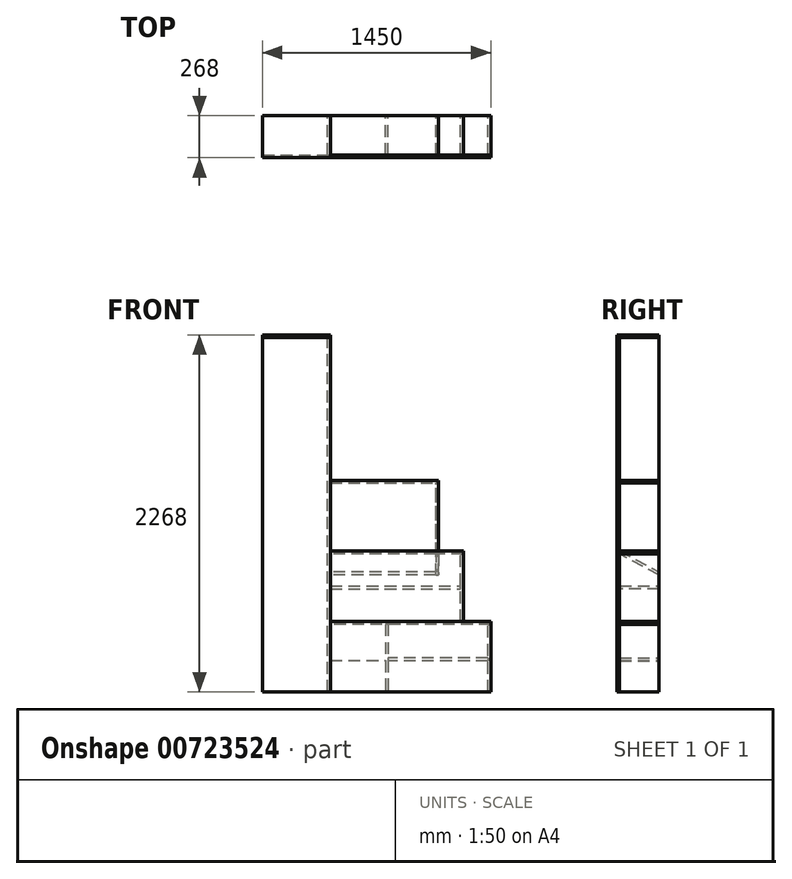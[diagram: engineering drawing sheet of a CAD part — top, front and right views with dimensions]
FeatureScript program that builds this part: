
annotation { "Feature Type Name" : "Feature", "Feature Type Description" : "" }
export const myFeature = defineFeature(function(context is Context, id is Id, definition is map)
    precondition{}
    {
        {
            var Q0;
            Q0=qCreatedBy(makeId("Front.planeOp"),FACE);
            var sketch = newSketch(context, id + "F0", { "sketchPlane" : qUnion([Q0])});
            skLineSegment(sketch, "E0.bottom", {"start": v(0, 0) * mm, "end": v(430, 0) * mm});
            skLineSegment(sketch, "E0.top", {"start": v(0, 2250) * mm, "end": v(430, 2250) * mm});
            skLineSegment(sketch, "E0.left", {"start": v(0, 0) * mm, "end": v(0, 2250) * mm});
            skLineSegment(sketch, "E0.right", {"start": v(430, 0) * mm, "end": v(430, 2250) * mm});
            skSolve(sketch);
        }
        {
            var Q0;
            Q0=qCreatedBy(makeId("Front.planeOp"),FACE);
            var sketch = newSketch(context, id + "F1", { "sketchPlane" : qUnion([Q0])});
            skLineSegment(sketch, "E1.bottom", {"start": v(430, 0) * mm, "end": v(1450, 0) * mm});
            skLineSegment(sketch, "E1.top", {"start": v(430, 448) * mm, "end": v(1450, 448) * mm});
            skLineSegment(sketch, "E1.left", {"start": v(430, 0) * mm, "end": v(430, 448) * mm});
            skLineSegment(sketch, "E1.right", {"start": v(1450, 0) * mm, "end": v(1450, 448) * mm});
            skSolve(sketch);
        }
        {
            var Q0;
            Q0=qCreatedBy(makeId("Front.planeOp"),FACE);
            var sketch = newSketch(context, id + "F2", { "sketchPlane" : qUnion([Q0])});
            skLineSegment(sketch, "E2.bottom", {"start": v(430, 448) * mm, "end": v(1275, 448) * mm});
            skLineSegment(sketch, "E2.top", {"start": v(430, 896) * mm, "end": v(1275, 896) * mm});
            skLineSegment(sketch, "E2.left", {"start": v(430, 448) * mm, "end": v(430, 896) * mm});
            skLineSegment(sketch, "E2.right", {"start": v(1275, 448) * mm, "end": v(1275, 896) * mm});
            skSolve(sketch);
        }
        {
            var Q0;
            Q0=qCreatedBy(makeId("Front.planeOp"),FACE);
            var sketch = newSketch(context, id + "F3", { "sketchPlane" : qUnion([Q0])});
            skLineSegment(sketch, "E3.bottom", {"start": v(430, 896) * mm, "end": v(1118, 896) * mm});
            skLineSegment(sketch, "E3.top", {"start": v(430, 1344) * mm, "end": v(1118, 1344) * mm});
            skLineSegment(sketch, "E3.left", {"start": v(430, 896) * mm, "end": v(430, 1344) * mm});
            skLineSegment(sketch, "E3.right", {"start": v(1118, 896) * mm, "end": v(1118, 1344) * mm});
            skSolve(sketch);
        }
        {
            var Q0;
            Q0=makeQuery(id+"F3.imprint","IMPRINT",FACE,{"disambiguationData":[TD([[makeQuery(id+"F3.imprint","IMPRINT",EDGE,{"derivedFrom":sQuery(id+"F3.wireOp",EDGE,"E3.bottom")}),1.0]])]});
            var Q1;
            Q1=makeQuery(id+"F2.imprint","IMPRINT",FACE,{"disambiguationData":[TD([[makeQuery(id+"F2.imprint","IMPRINT",EDGE,{"derivedFrom":sQuery(id+"F2.wireOp",EDGE,"E2.bottom")}),1.0]])]});
            var Q2;
            Q2=makeQuery(id+"F1.imprint","IMPRINT",FACE,{"disambiguationData":[TD([[makeQuery(id+"F1.imprint","IMPRINT",EDGE,{"derivedFrom":sQuery(id+"F1.wireOp",EDGE,"E1.bottom")}),1.0]])]});
            var Q3;
            Q3=makeQuery(id+"F0.imprint","IMPRINT",FACE,{"disambiguationData":[TD([[makeQuery(id+"F0.imprint","IMPRINT",EDGE,{"derivedFrom":sQuery(id+"F0.wireOp",EDGE,"E0.bottom")}),1.0]])]});
            extrude(context, id + "F4", {"entities" : qUnion([Q0, Q1, Q2, Q3]), "depth" : 18 * mm, "offsetDistance" : 25 * mm});
        }
        {
            var Q0;
            Q0=makeQuery(id+"F4.opExtrude","SWEPT_FACE",FACE,{"disambiguationData":[OSD([sQuery(id+"F0.wireOp",EDGE,"E0.right")])]});
            var sketch = newSketch(context, id + "F5", { "sketchPlane" : qUnion([Q0])});
            skLineSegment(sketch, "E4.bottom", {"start": v(0, 0) * mm, "end": v(250, 0) * mm});
            skLineSegment(sketch, "E4.top", {"start": v(0, 2250) * mm, "end": v(250, 2250) * mm});
            skLineSegment(sketch, "E4.left", {"start": v(0, 0) * mm, "end": v(0, 2250) * mm});
            skLineSegment(sketch, "E4.right", {"start": v(250, 0) * mm, "end": v(250, 2250) * mm});
            skSolve(sketch);
        }
        {
            var Q0;
            Q0=makeQuery(id+"F5.imprint","IMPRINT",FACE,{"disambiguationData":[TD([[makeQuery(id+"F5.imprint","IMPRINT",EDGE,{"derivedFrom":sQuery(id+"F5.wireOp",EDGE,"E4.bottom")}),1.0]])]});
            extrude(context, id + "F6", {"entities" : qUnion([Q0]), "oppositeDirection" : true, "depth" : 18 * mm, "offsetDistance" : 25 * mm});
        }
        {
            var Q0;
            Q0=makeQuery(id+"F4.opExtrude","SWEPT_FACE",FACE,{"disambiguationData":[OSD([sQuery(id+"F2.wireOp",EDGE,"E2.right")])]});
            var sketch = newSketch(context, id + "F7", { "sketchPlane" : qUnion([Q0])});
            skLineSegment(sketch, "E5.bottom", {"start": v(0, 448) * mm, "end": v(250, 448) * mm});
            skLineSegment(sketch, "E5.top", {"start": v(0, 878) * mm, "end": v(250, 878) * mm});
            skLineSegment(sketch, "E5.left", {"start": v(0, 448) * mm, "end": v(0, 878) * mm});
            skLineSegment(sketch, "E5.right", {"start": v(250, 448) * mm, "end": v(250, 878) * mm});
            skSolve(sketch);
        }
        {
            var Q0;
            Q0 = qSketchRegion(id + "F7", true);
            extrude(context, id + "F8", {"entities" : qUnion([Q0]), "oppositeDirection" : true, "depth" : 18 * mm, "offsetDistance" : 25 * mm});
        }
        {
            var Q0;
            Q0=makeQuery(id+"F8.opExtrude","SWEPT_FACE",FACE,{"disambiguationData":[OSD([sQuery(id+"F7.wireOp",EDGE,"E5.bottom")])]});
            var sketch = newSketch(context, id + "F9", { "sketchPlane" : qUnion([Q0])});
            skLineSegment(sketch, "E6.bottom", {"start": v(1450, 0) * mm, "end": v(430, 0) * mm});
            skLineSegment(sketch, "E6.top", {"start": v(1450, -250) * mm, "end": v(430, -250) * mm});
            skLineSegment(sketch, "E6.left", {"start": v(1450, 0) * mm, "end": v(1450, -250) * mm});
            skLineSegment(sketch, "E6.right", {"start": v(430, 0) * mm, "end": v(430, -250) * mm});
            skSolve(sketch);
        }
        {
            var Q0;
            Q0 = qSketchRegion(id + "F9", true);
            extrude(context, id + "F10", {"entities" : qUnion([Q0]), "depth" : 18 * mm, "offsetDistance" : 25 * mm});
        }
        {
            var Q0;
            Q0=makeQuery(id+"F4.opExtrude","SWEPT_FACE",FACE,{"disambiguationData":[OSD([sQuery(id+"F1.wireOp",EDGE,"E1.right")])]});
            var sketch = newSketch(context, id + "F11", { "sketchPlane" : qUnion([Q0])});
            skLineSegment(sketch, "E7.bottom", {"start": v(0, 0) * mm, "end": v(250, 0) * mm});
            skLineSegment(sketch, "E7.top", {"start": v(0, 430) * mm, "end": v(250, 430) * mm});
            skLineSegment(sketch, "E7.left", {"start": v(0, 0) * mm, "end": v(0, 430) * mm});
            skLineSegment(sketch, "E7.right", {"start": v(250, 0) * mm, "end": v(250, 430) * mm});
            skSolve(sketch);
        }
        {
            var Q0;
            Q0 = qSketchRegion(id + "F11", true);
            extrude(context, id + "F12", {"entities" : qUnion([Q0]), "oppositeDirection" : true, "depth" : 18 * mm, "offsetDistance" : 25 * mm});
        }
        {
            var Q0;
            Q0=makeQuery(id+"FPP5edtGo1Gx8Hw_4.boolean.opBoolean","MERGE",FACE,{"derivedFrom":[makeQuery(id+"F4.opExtrude","SWEPT_FACE",FACE,{"disambiguationData":[OSD([sQuery(id+"F0.wireOp",EDGE,"E0.bottom")])]}),makeQuery(id+"FPP5edtGo1Gx8Hw_4.opExtrude","SWEPT_FACE",FACE,{"disambiguationData":[OSD([sQuery(id+"F5.wireOp",EDGE,"E4.bottom")])]})]});
            var sketch = newSketch(context, id + "F13", { "sketchPlane" : qUnion([Q0])});
            skLineSegment(sketch, "E8.bottom", {"start": v(430, 0) * mm, "end": v(780, 0) * mm});
            skLineSegment(sketch, "E8.top", {"start": v(430, -250) * mm, "end": v(780, -250) * mm});
            skLineSegment(sketch, "E8.left", {"start": v(430, 0) * mm, "end": v(430, -250) * mm});
            skLineSegment(sketch, "E8.right", {"start": v(780, 0) * mm, "end": v(780, -250) * mm});
            skSolve(sketch);
        }
        {
            var Q0;
            Q0=makeQuery(id+"F13.imprint","IMPRINT",FACE,{"disambiguationData":[TD([[makeQuery(id+"F13.imprint","IMPRINT",EDGE,{"derivedFrom":sQuery(id+"F13.wireOp",EDGE,"E8.bottom")}),-1.0]])]});
            extrude(context, id + "F14", {"entities" : qUnion([Q0]), "oppositeDirection" : true, "depth" : 200 * mm, "offsetDistance" : 25 * mm});
        }
        {
            var Q0;
            Q0=makeQuery(id+"FPP5edtGo1Gx8Hw_4.boolean.opBoolean","MERGE",FACE,{"derivedFrom":[makeQuery(id+"F4.opExtrude","SWEPT_FACE",FACE,{"disambiguationData":[OSD([sQuery(id+"F0.wireOp",EDGE,"E0.top")])]}),makeQuery(id+"FPP5edtGo1Gx8Hw_4.opExtrude","SWEPT_FACE",FACE,{"disambiguationData":[OSD([sQuery(id+"F5.wireOp",EDGE,"E4.top")])]})]});
            var sketch = newSketch(context, id + "F15", { "sketchPlane" : qUnion([Q0])});
            skLineSegment(sketch, "E9.bottom", {"start": v(430, -18) * mm, "end": v(0, -18) * mm});
            skLineSegment(sketch, "E9.top", {"start": v(430, 250) * mm, "end": v(0, 250) * mm});
            skLineSegment(sketch, "E9.left", {"start": v(430, -18) * mm, "end": v(430, 250) * mm});
            skLineSegment(sketch, "E9.right", {"start": v(0, -18) * mm, "end": v(0, 250) * mm});
            skSolve(sketch);
        }
        {
            var Q0;
            Q0 = qSketchRegion(id + "F15", true);
            extrude(context, id + "F16", {"entities" : qUnion([Q0]), "depth" : 18 * mm, "offsetDistance" : 25 * mm});
        }
        {
            var Q0;
            Q0=makeQuery(id+"F14.opExtrude","SWEPT_FACE",FACE,{"disambiguationData":[OSD([sQuery(id+"F13.wireOp",EDGE,"E8.right")])]});
            var sketch = newSketch(context, id + "F17", { "sketchPlane" : qUnion([Q0])});
            skLineSegment(sketch, "E10.bottom", {"start": v(250, 0) * mm, "end": v(0, 0) * mm});
            skLineSegment(sketch, "E10.top", {"start": v(250, 430) * mm, "end": v(0, 430) * mm});
            skLineSegment(sketch, "E10.left", {"start": v(250, 0) * mm, "end": v(250, 430) * mm});
            skLineSegment(sketch, "E10.right", {"start": v(0, 0) * mm, "end": v(0, 430) * mm});
            skSolve(sketch);
        }
        {
            var Q0;
            Q0 = qSketchRegion(id + "F17", true);
            extrude(context, id + "F18", {"entities" : qUnion([Q0]), "depth" : 18 * mm, "offsetDistance" : 25 * mm});
        }
        {
            var Q0;
            Q0=makeQuery(id+"F18.opExtrude","CAP_FACE",FACE,{"disambiguationData":[OSD([sQuery(id+"F17.wireOp",EDGE,"E10.bottom"),sQuery(id+"F17.wireOp",EDGE,"E10.top"),sQuery(id+"F17.wireOp",EDGE,"E10.left"),sQuery(id+"F17.wireOp",EDGE,"E10.right")])],"isStart":false});
            var sketch = newSketch(context, id + "F19", { "sketchPlane" : qUnion([Q0])});
            skLineSegment(sketch, "E11.bottom", {"start": v(0, 215) * mm, "end": v(250, 215) * mm});
            skLineSegment(sketch, "E11.top", {"start": v(0, 197) * mm, "end": v(250, 197) * mm});
            skLineSegment(sketch, "E11.left", {"start": v(0, 215) * mm, "end": v(0, 197) * mm});
            skLineSegment(sketch, "E11.right", {"start": v(250, 215) * mm, "end": v(250, 197) * mm});
            skSolve(sketch);
        }
        {
            var Q0;
            Q0=makeQuery(id+"F19.imprint","IMPRINT",FACE,{"disambiguationData":[TD([[makeQuery(id+"F19.imprint","IMPRINT",EDGE,{"derivedFrom":sQuery(id+"F19.wireOp",EDGE,"E11.bottom")}),-1.0]])]});
            extrude(context, id + "F20", {"entities" : qUnion([Q0]), "endBound" : BoundingType.UP_TO_NEXT, "depth" : 25 * mm, "offsetDistance" : 25 * mm});
        }
        {
            var Q0;
            Q0=makeQuery(id+"F8.opExtrude","CAP_FACE",FACE,{"disambiguationData":[OSD([sQuery(id+"F7.wireOp",EDGE,"E5.bottom"),sQuery(id+"F7.wireOp",EDGE,"E5.top"),sQuery(id+"F7.wireOp",EDGE,"E5.left"),sQuery(id+"F7.wireOp",EDGE,"E5.right")])],"isStart":false});
            var sketch = newSketch(context, id + "F21", { "sketchPlane" : qUnion([Q0])});
            skLineSegment(sketch, "E12.bottom", {"start": v(0, 654) * mm, "end": v(-250, 654) * mm});
            skLineSegment(sketch, "E12.top", {"start": v(-250, 672) * mm, "end": v(0, 672) * mm});
            skLineSegment(sketch, "E12.left", {"start": v(-250, 654) * mm, "end": v(-250, 672) * mm});
            skLineSegment(sketch, "E12.right", {"start": v(0, 654) * mm, "end": v(0, 672) * mm});
            skSolve(sketch);
        }
        {
            var Q0;
            Q0=makeQuery(id+"F21.imprint","IMPRINT",FACE,{"disambiguationData":[TD([[makeQuery(id+"F21.imprint","IMPRINT",EDGE,{"derivedFrom":sQuery(id+"F21.wireOp",EDGE,"E12.bottom")}),-1.0]])]});
            extrude(context, id + "F22", {"entities" : qUnion([Q0]), "endBound" : BoundingType.UP_TO_NEXT, "depth" : 25 * mm, "offsetDistance" : 25 * mm});
        }
        {
            var Q0;
            Q0=makeQuery(id+"F5.imprint","IMPRINT",FACE,{"disambiguationData":[TD([[makeQuery(id+"F5.imprint","IMPRINT",EDGE,{"derivedFrom":sQuery(id+"F5.wireOp",EDGE,"E4.bottom")}),1.0]])]});
            var sketch = newSketch(context, id + "F23", { "sketchPlane" : qUnion([Q0])});
            skLineSegment(sketch, "E13", {"start": v(250, 763.07) * mm, "end": v(250, 742.69) * mm});
            skLineSegment(sketch, "E14", {"start": v(250, 742.69) * mm, "end": v(0, 875.61) * mm});
            skLineSegment(sketch, "E15", {"start": v(0, 875.61) * mm, "end": v(0, 896) * mm});
            skLineSegment(sketch, "E16", {"start": v(0, 896) * mm, "end": v(250, 763.07) * mm});
            skSolve(sketch);
        }
        {
            var Q0;
            Q0=makeQuery(id+"F4.opExtrude","SWEPT_FACE",FACE,{"disambiguationData":[OSD([sQuery(id+"F3.wireOp",EDGE,"E3.top")])]});
            var sketch = newSketch(context, id + "F24", { "sketchPlane" : qUnion([Q0])});
            skLineSegment(sketch, "E17.bottom", {"start": v(430, 0) * mm, "end": v(1118, 0) * mm});
            skLineSegment(sketch, "E17.top", {"start": v(430, 250) * mm, "end": v(1118, 250) * mm});
            skLineSegment(sketch, "E17.left", {"start": v(430, 0) * mm, "end": v(430, 250) * mm});
            skLineSegment(sketch, "E17.right", {"start": v(1118, 0) * mm, "end": v(1118, 250) * mm});
            skSolve(sketch);
        }
        {
            var Q0;
            Q0 = qSketchRegion(id + "F24", true);
            extrude(context, id + "F25", {"entities" : qUnion([Q0]), "oppositeDirection" : true, "depth" : 18 * mm, "offsetDistance" : 25 * mm});
        }
        {
            var Q0;
            Q0=makeQuery(id+"F4.opExtrude","SWEPT_FACE",FACE,{"disambiguationData":[OSD([sQuery(id+"F3.wireOp",EDGE,"E3.right")])]});
            var sketch = newSketch(context, id + "F26", { "sketchPlane" : qUnion([Q0])});
            skLineSegment(sketch, "E18", {"start": v(0, 1326) * mm, "end": v(0, 896) * mm});
            skLineSegment(sketch, "E19", {"start": v(0, 875.61) * mm, "end": v(250, 742.69) * mm});
            skLineSegment(sketch, "E20", {"start": v(250, 742.69) * mm, "end": v(250, 1326) * mm});
            skLineSegment(sketch, "E21", {"start": v(250, 1326) * mm, "end": v(0, 1326) * mm});
            skLineSegment(sketch, "E22", {"start": v(0, 875.61) * mm, "end": v(0, 896) * mm});
            skSolve(sketch);
        }
        {
            var Q0;
            Q0 = qSketchRegion(id + "F26", true);
            extrude(context, id + "F27", {"entities" : qUnion([Q0]), "oppositeDirection" : true, "depth" : 18 * mm, "offsetDistance" : 25 * mm});
        }
        {
            var Q0;
            Q0=makeQuery(id+"F2.imprint","IMPRINT",FACE,{"disambiguationData":[TD([[makeQuery(id+"F2.imprint","IMPRINT",EDGE,{"derivedFrom":sQuery(id+"F2.wireOp",EDGE,"E2.bottom")}),1.0]])]});
            var sketch = newSketch(context, id + "F28", { "sketchPlane" : qUnion([Q0])});
            skLineSegment(sketch, "E23.bottom", {"start": v(1275, 896) * mm, "end": v(1118, 896) * mm});
            skLineSegment(sketch, "E23.top", {"start": v(1275, 878) * mm, "end": v(1118, 878) * mm});
            skLineSegment(sketch, "E23.left", {"start": v(1275, 896) * mm, "end": v(1275, 878) * mm});
            skLineSegment(sketch, "E23.right", {"start": v(1118, 896) * mm, "end": v(1118, 878) * mm});
            skSolve(sketch);
        }
        {
            var Q0;
            Q0=makeQuery(id+"F23.imprint","IMPRINT",FACE,{"disambiguationData":[TD([[makeQuery(id+"F23.imprint","IMPRINT",EDGE,{"derivedFrom":sQuery(id+"F23.wireOp",EDGE,"E13")}),1.0]])]});
            var Q1;
            Q1=makeQuery(id+"F27.opExtrude","CAP_FACE",FACE,{"disambiguationData":[OSD([sQuery(id+"F26.wireOp",EDGE,"E18"),sQuery(id+"F26.wireOp",EDGE,"E19"),sQuery(id+"F26.wireOp",EDGE,"E20"),sQuery(id+"F26.wireOp",EDGE,"E21"),sQuery(id+"F26.wireOp",EDGE,"E22")])],"isStart":false});
            extrude(context, id + "F29", {"entities" : qUnion([Q0]), "endBound" : BoundingType.UP_TO_SURFACE, "depth" : 25 * mm, "endBoundEntityFace" : qUnion([Q1]), "offsetDistance" : 25 * mm});
        }
        {
            var Q0;
            Q0 = qSketchRegion(id + "F28", true);
            var Q1;
            Q1=makeQuery(id+"F8.opExtrude","SWEPT_FACE",FACE,{"disambiguationData":[OSD([sQuery(id+"F7.wireOp",EDGE,"E5.right")])]});
            extrude(context, id + "F30", {"entities" : qUnion([Q0]), "endBound" : BoundingType.UP_TO_SURFACE, "oppositeDirection" : true, "depth" : 25 * mm, "endBoundEntityFace" : qUnion([Q1]), "offsetDistance" : 25 * mm});
        }
        {
            var Q0;
            Q0 = qSketchRegion(id + "F28", true);
            var Q1;
            Q1 = qConstructionFilter(qBodyType(qCreatedBy(id + "F28" ,EDGE), BodyType.WIRE), ConstructionObject.NO);
            var Q2;
            Q2=makeQuery(id+"F8.opExtrude","SWEPT_FACE",FACE,{"disambiguationData":[OSD([sQuery(id+"F7.wireOp",EDGE,"E5.right")])]});
            extrude(context, id + "F31", {"entities" : qUnion([Q0]), "surfaceEntities" : qUnion([Q1]), "endBound" : BoundingType.UP_TO_SURFACE, "oppositeDirection" : true, "depth" : 25 * mm, "endBoundEntityFace" : qUnion([Q2]), "offsetDistance" : 25 * mm});
        }
        {
            var Q0;
            Q0=makeQuery(id+"F31.opExtrude","SWEPT_BODY",BODY,{"disambiguationData":[OSD([sQuery(id+"F28.wireOp",EDGE,"E23.bottom"),sQuery(id+"F28.wireOp",EDGE,"E23.top"),sQuery(id+"F28.wireOp",EDGE,"E23.left"),sQuery(id+"F28.wireOp",EDGE,"E23.right")])]});
            deleteBodies(context, id + "F32", {"entities" : qUnion([Q0])});
        }
    });
